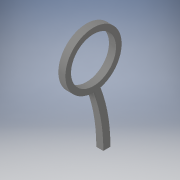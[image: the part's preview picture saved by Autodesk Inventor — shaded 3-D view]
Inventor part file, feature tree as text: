
AUTODESK INVENTOR PART (.ipt)
format: ipt  version: 2019.2 (Build 232265000, 265)  size: 141,312 bytes
history: native  units: in
note: dims shown in document units (in); Inventor stores cm internally (conversion verified against a paired STEP export)
features: extrude x3, sketch x3
ambient origin geometry x8: Origin, YZ Plane, XZ Plane, XY Plane, X Axis, Y Axis, Z Axis, Center Point
bodies: Solid1 (feature_tree)
feature tree (6):
  extrude  "Extrusion1"  Depth=0.25in TaperAngle=0.0deg
  extrude  "Extrusion2"  Depth=0.25in TaperAngle=0.0deg
  extrude  "Extrusion3"  [1 undecoded]
  sketch  "Sketch1"  dims[d7=1.6in d8=0.25in d9=0.0in]
  sketch  "Sketch2"  dims[d13=1.9853in d24=0.25in d25=0.0in]
  sketch  "Sketch3"  dims[d27=0.25in d28=0.0in]
note: 1 required parameter value undecoded (feature->parameter linkage not recoverable at this tier; creation-order binding heuristic only, values carry confidence <= 0.55)
